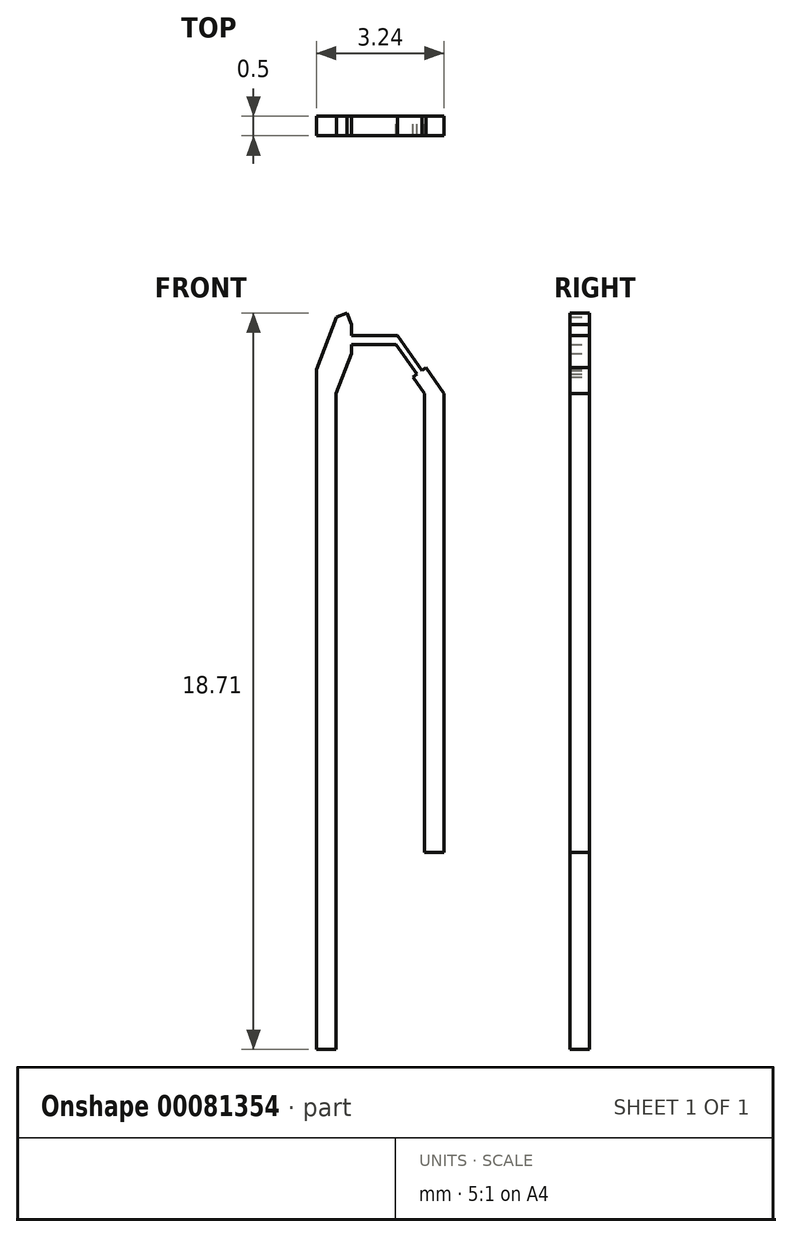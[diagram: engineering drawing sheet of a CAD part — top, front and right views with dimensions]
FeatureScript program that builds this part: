
annotation { "Feature Type Name" : "Feature", "Feature Type Description" : "" }
export const myFeature = defineFeature(function(context is Context, id is Id, definition is map)
    precondition{}
    {
        {
            var Q0;
            Q0=qCreatedBy(makeId("Front.planeOp"),FACE);
            var sketch = newSketch(context, id + "F0", { "sketchPlane" : qUnion([Q0])});
            skLineSegment(sketch, "E0", {"start": v(-3, 0) * mm, "end": v(3, 0) * mm, "construction": true});
            skLineSegment(sketch, "E1", {"start": v(-1.53, -15) * mm, "end": v(-1.53, 2.28) * mm});
            skLineSegment(sketch, "E2", {"start": v(-1.53, 2.28) * mm, "end": v(-1.02, 3.61) * mm});
            skLineSegment(sketch, "E3", {"start": v(-1.02, 3.61) * mm, "end": v(-0.75, 3.7) * mm});
            skLineSegment(sketch, "E4", {"start": v(-0.75, 3.7) * mm, "end": v(-0.65, 3.4) * mm});
            skLineSegment(sketch, "E5", {"start": v(-0.65, 3.4) * mm, "end": v(-0.65, 3.14) * mm});
            skLineSegment(sketch, "E6", {"start": v(-0.65, 2.68) * mm, "end": v(-1.03, 1.67) * mm});
            skLineSegment(sketch, "E7", {"start": v(-1.03, 1.67) * mm, "end": v(-1.03, -15) * mm});
            skLineSegment(sketch, "E8", {"start": v(-1.03, -15) * mm, "end": v(-1.53, -15) * mm});
            skLineSegment(sketch, "E9", {"start": v(1.2, -10) * mm, "end": v(1.2, 1.67) * mm});
            skPoint(sketch, "E9.startSnap0", {"position": v(-1.28, -15) * mm});
            skLineSegment(sketch, "E10", {"start": v(1.2, 1.67) * mm, "end": v(0.92, 2.08) * mm});
            skLineSegment(sketch, "E11", {"start": v(0.92, 2.08) * mm, "end": v(1.02, 2.15) * mm});
            skLineSegment(sketch, "E12", {"start": v(1.25, 2.32) * mm, "end": v(1.7, 1.67) * mm});
            skLineSegment(sketch, "E13", {"start": v(1.7, 1.67) * mm, "end": v(1.7, -10) * mm});
            skLineSegment(sketch, "E14", {"start": v(1.7, -10) * mm, "end": v(1.2, -10) * mm});
            skLineSegment(sketch, "E15", {"start": v(-0.65, 2.91) * mm, "end": v(0.49, 2.91) * mm});
            skLineSegment(sketch, "E16", {"start": v(0.49, 2.91) * mm, "end": v(1.02, 2.15) * mm});
            skLineSegment(sketch, "E17", {"start": v(-0.65, 3.14) * mm, "end": v(0.52, 3.14) * mm});
            skLineSegment(sketch, "E18", {"start": v(0.52, 3.14) * mm, "end": v(1.15, 2.24) * mm});
            skLineSegment(sketch, "E19.trimOffspring", {"start": v(-0.65, 2.91) * mm, "end": v(-0.65, 2.68) * mm});
            skLineSegment(sketch, "E20.trimOffspring", {"start": v(1.15, 2.24) * mm, "end": v(1.25, 2.32) * mm});
            skSolve(sketch);
        }
        {
            var Q0;
            Q0=qSketchRegion(id+"F0",true);
            extrude(context, id + "F1", {"entities" : qUnion([Q0]), "endBound" : BoundingType.SYMMETRIC, "depth" : 0.5 * mm});
        }
    });
